# Revit family: pm-(h)rp40_80fa17_50Hz
name_source: partatom
category: 機械設備
units: mm (PartAtom-declared; Revit-internal decimal feet)

## family parameters
OmniClass タイトル = Split System Air Conditioning Units
OmniClass 番号 = 23.75.10.24.21.27.27
パーツ タイプ = 標準
ロード時にボイドで切り取り = いいえ
丸型コネクタ寸法 = 直径を使用
作業面ベース = いいえ
共有 = いいえ
常に垂直 = はい
部屋計算ポイント = はい

## types (8) — shared parameters
Clearance Back = 150
Clearance Bottom = 500  [stored 1.64042 ft]
Clearance Front = 150
Clearance Left = 1500  [stored 4.92126 ft]
Clearance Right = 20  [stored 0.0656168 ft]
Clearance Top = 230  [stored 0.754593 ft]
Depth = 1112  [stored 3.64829 ft]
Height = 225  [stored 0.738189 ft]
IfcExportAs = IfcUnitaryEquipmentType
IfcExportType = AIRCONDITIONINGUNIT
OmniClassCode = 23-33 17 13 11
Panel Depth = 1340  [stored 4.39633 ft]
Panel Height = 20  [stored 0.0656168 ft]
Panel Width = 800  [stored 2.62467 ft]
S_H = 230  [stored 0.754593 ft]
URL = https://www.mitsubishielectric.co.jp
Uniclass2015Code = Pr_70_65_03_84
Uniclass2015Title = Split coil remote air cooled condensing units
Uniclass2015Version = Systems v1.9
Width = 724  [stored 2.37533 ft]
ケーブルサイズ = 0 mm
サービススペース = はい
ドレン管径 = 25 mm
ドレン管径 (外径) = 32 mm
ドレン管高さ = 159  [stored 0.521654 ft]
パネルマテリアル = <カテゴリ別>
仕様書バージョン = Version1.0
企業コード = 108420
冷媒ガス管長さ = 72  [stored 0.23622 ft]
冷媒ガス管高さ = 141
冷媒液管長さ = 72  [stored 0.23622 ft]
冷媒液管高さ = 171  [stored 0.561024 ft]
冷媒管径 = 100 mm
冷媒高低圧ガス管径 = 0 mm
分類コード = 50053003123030
加湿給水管径 = 0 mm
参照している仕様書等のバージョン = 公共建築工事標準仕様書（機械設備工事編）平成31年度版
吊りボルト_H = 117  [stored 0.383858 ft]
吊り位置X = 510  [stored 1.67323 ft]
吊り位置Y = 1173  [stored 3.84843 ft]
周波数 = 50 Hz
呼称 = パッケージ形空気調和機_室内機
始動方式 = 直入
形式 = 1方向天井カセット形
推奨ブレーカー容量 = 0 A
本体マテリアル = <カテゴリ別>
極数 = 1
法定耐用年数 = 6
消費電力_加湿器 = 0.00 kW
消費電力_電気ヒーター = 0.00 kW
発停方法 = 付属スイッチ
相 = 1
積算_科目 = 1 空気調和設備
符号 = PAC-CK1
製品リリース年月 = 2021/5/10
製品出荷対象 = 国内
製造元 = 三菱電機株式会社
設置方法 = カセット形
設計冷房能力 = 0 kW
設計冷房能力_顕熱 = 0 kW
設計暖房能力 = 0.00 kW
説明 = 店舗・事務所用パッケージエアコン(Mr.SLIM) [本体]1方向天井カセット形
負荷分類 = 3_ファン類
運転質量 = 0.00 kg
電圧 = 200 V
電圧_電気ヒーター = 0 V
zero-valued in all types: 有効加湿量

## per-type parameters (varying)
- 天井1方向_PM-RP40FA17: MAX風量=900.0 m³/h; MID風量=840.0 m³/h; MID風量2=720.0 m³/h; MIN風量=660.0 m³/h; 価格=275000 $; 冷媒ガス管径=13 mm; 冷媒液管径=6 mm; 冷媒管径符号=Ac; 冷房能力=3.6 kW; 暖房能力=4.00 kW; 構成品番=PM-RP40FA; 消費電力=0.08 kW; 消費電力_冷房=0.08 kW; 消費電力_暖房=0.07 kW; 製品質量=31.50 kg; 質量=37.80 kg; 電動機出力_送風機=0.09 kW; 電源_H=60  [stored 0.19685 ft]; 音響パワーレベル(dB)=55; 音響パワーレベル（中1）(dB)=52; 音響パワーレベル（中2）(dB)=50; 音響パワーレベル（弱）(dB)=47; 風量=900.0 m³/h; 風量（中）（m3／min）=14; 風量（弱）（m3／min）=12; 風量（強）（m3／min）=15; 風量（静）（m3／min）=11
- 天井1方向_PM-RP45FA17: MAX風量=900.0 m³/h; MID風量=840.0 m³/h; MID風量2=720.0 m³/h; MIN風量=660.0 m³/h; 価格=283000 $; 冷媒ガス管径=13 mm; 冷媒液管径=6 mm; 冷媒管径符号=Ac; 冷房能力=4 kW; 暖房能力=4.50 kW; 構成品番=PM-RP45FA; 消費電力=0.08 kW; 消費電力_冷房=0.08 kW; 消費電力_暖房=0.07 kW; 製品質量=31.50 kg; 質量=37.80 kg; 電動機出力_送風機=0.09 kW; 電源_H=60  [stored 0.19685 ft]; 音響パワーレベル(dB)=55; 音響パワーレベル（中1）(dB)=52; 音響パワーレベル（中2）(dB)=50; 音響パワーレベル（弱）(dB)=47; 風量=900.0 m³/h; 風量（中）（m3／min）=14; 風量（弱）（m3／min）=12; 風量（強）（m3／min）=15; 風量（静）（m3／min）=11
- 天井1方向_PM-RP50FA17: MAX風量=900.0 m³/h; MID風量=840.0 m³/h; MID風量2=720.0 m³/h; MIN風量=660.0 m³/h; 価格=306000 $; 冷媒ガス管径=13 mm; 冷媒液管径=6 mm; 冷媒管径符号=Ac; 冷房能力=4.5 kW; 暖房能力=5.00 kW; 構成品番=PM-RP50FA; 消費電力=0.08 kW; 消費電力_冷房=0.08 kW; 消費電力_暖房=0.07 kW; 製品質量=31.50 kg; 質量=37.80 kg; 電動機出力_送風機=0.09 kW; 電源_H=60  [stored 0.19685 ft]; 音響パワーレベル(dB)=55; 音響パワーレベル（中1）(dB)=52; 音響パワーレベル（中2）(dB)=50; 音響パワーレベル（弱）(dB)=47; 風量=900.0 m³/h; 風量（中）（m3／min）=14; 風量（弱）（m3／min）=12; 風量（強）（m3／min）=15; 風量（静）（m3／min）=11
- 天井1方向_PM-RP56FA17: MAX風量=1020.0 m³/h; MID風量=960.0 m³/h; MID風量2=900.0 m³/h; MIN風量=840.0 m³/h; 価格=317000 $; 冷媒ガス管径=13 mm; 冷媒液管径=6 mm; 冷媒管径符号=Ac; 冷房能力=5 kW; 暖房能力=5.60 kW; 構成品番=PM-RP56FA; 消費電力=0.08 kW; 消費電力_冷房=0.08 kW; 消費電力_暖房=0.07 kW; 製品質量=32.50 kg; 質量=39.00 kg; 電動機出力_送風機=0.10 kW; 電源_H=60  [stored 0.19685 ft]; 音響パワーレベル(dB)=55; 音響パワーレベル（中1）(dB)=53; 音響パワーレベル（中2）(dB)=51; 音響パワーレベル（弱）(dB)=50; 風量=1020.0 m³/h; 風量（中）（m3／min）=16; 風量（弱）（m3／min）=15; 風量（強）（m3／min）=17; 風量（静）（m3／min）=14
- 天井1方向_PM-RP63FA17: MAX風量=1140.0 m³/h; MID風量=1020.0 m³/h; MID風量2=960.0 m³/h; MIN風量=840.0 m³/h; 価格=330000 $; 冷媒ガス管径=13 mm; 冷媒液管径=6 mm; 冷媒管径符号=Ac; 冷房能力=5.6 kW; 暖房能力=6.30 kW; 構成品番=PM-RP63FA; 消費電力=0.09 kW; 消費電力_冷房=0.09 kW; 消費電力_暖房=0.08 kW; 製品質量=32.50 kg; 質量=39.00 kg; 電動機出力_送風機=0.10 kW; 電源_H=60  [stored 0.19685 ft]; 音響パワーレベル(dB)=56; 音響パワーレベル（中1）(dB)=54; 音響パワーレベル（中2）(dB)=52; 音響パワーレベル（弱）(dB)=50; 風量=1140.0 m³/h; 風量（中）（m3／min）=17; 風量（弱）（m3／min）=16; 風量（強）（m3／min）=19; 風量（静）（m3／min）=14
- 天井1方向_PM-RP71FA17: MAX風量=1200.0 m³/h; MID風量=1080.0 m³/h; MID風量2=960.0 m³/h; MIN風量=840.0 m³/h; 価格=336000 $; 冷媒ガス管径=16 mm; 冷媒液管径=10 mm; 冷媒管径符号=Bd; 冷房能力=6.3 kW; 暖房能力=7.00 kW; 構成品番=PM-RP71FA; 消費電力=0.10 kW; 消費電力_冷房=0.10 kW; 消費電力_暖房=0.09 kW; 製品質量=32.50 kg; 質量=39.00 kg; 電動機出力_送風機=0.10 kW; 電源_H=60  [stored 0.19685 ft]; 音響パワーレベル(dB)=58; 音響パワーレベル（中1）(dB)=55; 音響パワーレベル（中2）(dB)=53; 音響パワーレベル（弱）(dB)=51; 風量=1200.0 m³/h; 風量（中）（m3／min）=18; 風量（弱）（m3／min）=16; 風量（強）（m3／min）=20; 風量（静）（m3／min）=14
- 天井1方向_PM-RP80FA17: MAX風量=1200.0 m³/h; MID風量=1080.0 m³/h; MID風量2=960.0 m³/h; MIN風量=840.0 m³/h; 価格=352000 $; 冷媒ガス管径=16 mm; 冷媒液管径=10 mm; 冷媒管径符号=Bd; 冷房能力=7.1 kW; 暖房能力=8.00 kW; 構成品番=PM-RP80FA; 消費電力=0.10 kW; 消費電力_冷房=0.10 kW; 消費電力_暖房=0.09 kW; 製品質量=32.50 kg; 質量=39.00 kg; 電動機出力_送風機=0.10 kW; 電源_H=0  [stored 0 ft]; 音響パワーレベル(dB)=58; 音響パワーレベル（中1）(dB)=55; 音響パワーレベル（中2）(dB)=53; 音響パワーレベル（弱）(dB)=51; 風量=1200.0 m³/h; 風量（中）（m3／min）=18; 風量（弱）（m3／min）=16; 風量（強）（m3／min）=20; 風量（静）（m3／min）=14
- 天井1方向_PM-HRP80FA17: MAX風量=1200.0 m³/h; MID風量=1080.0 m³/h; MID風量2=960.0 m³/h; MIN風量=840.0 m³/h; 価格=358000 $; 冷媒ガス管径=16 mm; 冷媒液管径=10 mm; 冷媒管径符号=Bd; 冷房能力=7.1 kW; 暖房能力=8.00 kW; 構成品番=PM-HRP80FA; 消費電力=0.11 kW; 消費電力_冷房=0.11 kW; 消費電力_暖房=0.10 kW; 製品質量=33.50 kg; 質量=40.20 kg; 電動機出力_送風機=0.10 kW; 電源_H=60  [stored 0.19685 ft]; 音響パワーレベル(dB)=59; 音響パワーレベル（中1）(dB)=55; 音響パワーレベル（中2）(dB)=53; 音響パワーレベル（弱）(dB)=51; 風量=1200.0 m³/h; 風量（中）（m3／min）=18; 風量（弱）（m3／min）=16; 風量（強）（m3／min）=20; 風量（静）（m3／min）=14

note: [stored X ft] marks values corroborated as IEEE doubles in the binary element streams (Revit-internal decimal feet)
